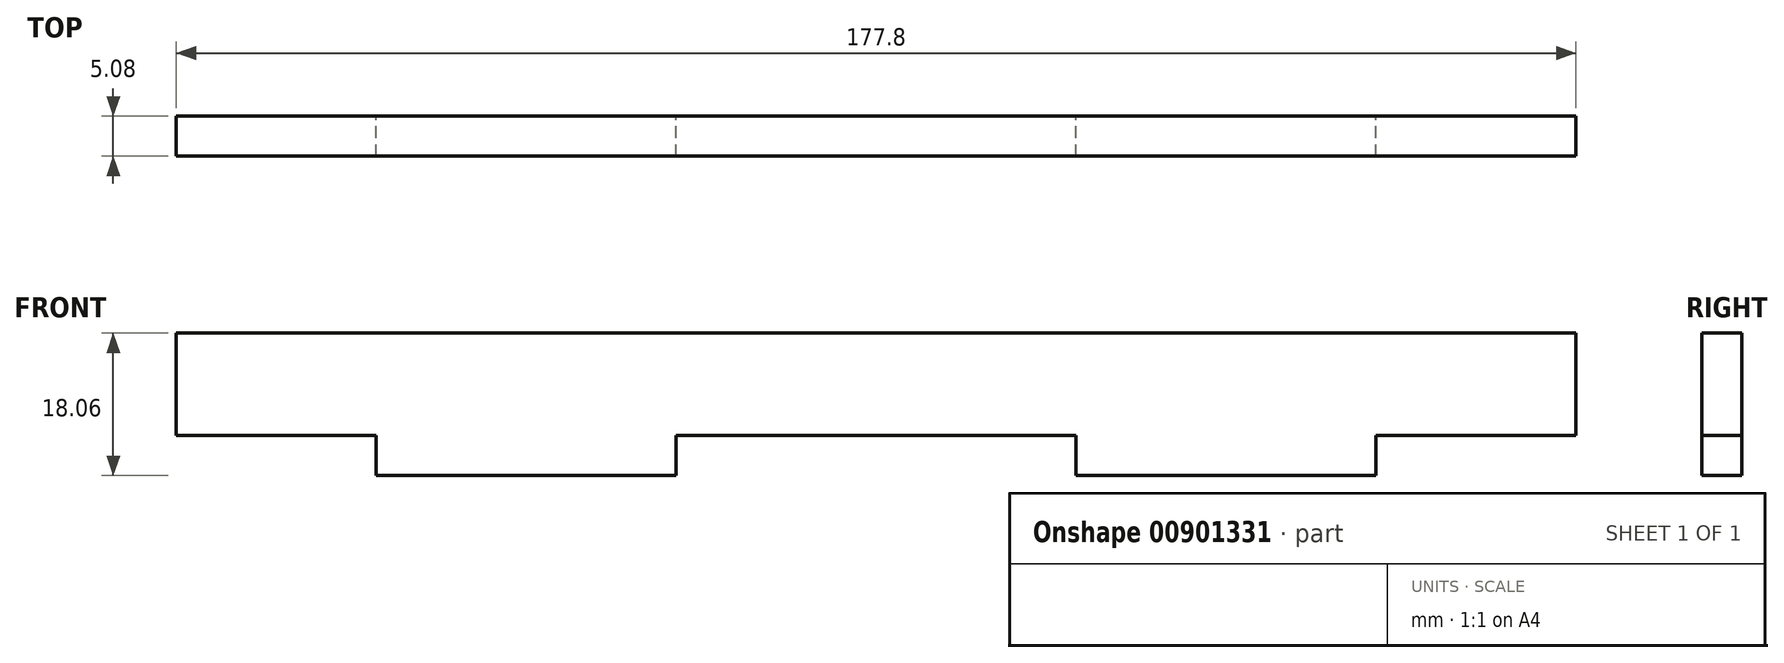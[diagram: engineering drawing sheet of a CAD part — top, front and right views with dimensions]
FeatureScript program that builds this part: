
annotation { "Feature Type Name" : "Feature", "Feature Type Description" : "" }
export const myFeature = defineFeature(function(context is Context, id is Id, definition is map)
    precondition{}
    {
        {
            var Q0;
            Q0=qCreatedBy(makeId("Front.planeOp"),FACE);
            var sketch = newSketch(context, id + "F0", { "sketchPlane" : qUnion([Q0])});
            skLineSegment(sketch, "E0", {"start": v(0, 0) * mm, "end": v(-25.4, 0) * mm});
            skLineSegment(sketch, "E1", {"start": v(-25.4, 0) * mm, "end": v(-25.4, -5.08) * mm});
            skLineSegment(sketch, "E2", {"start": v(-25.4, -5.08) * mm, "end": v(-63.5, -5.08) * mm});
            skLineSegment(sketch, "E3", {"start": v(-63.5, -5.08) * mm, "end": v(-63.5, 0) * mm});
            skLineSegment(sketch, "E4.MirrorCS", {"start": v(0, 0) * mm, "end": v(25.4, 0) * mm});
            skLineSegment(sketch, "E5.MirrorCS", {"start": v(25.4, 0) * mm, "end": v(25.4, -5.08) * mm});
            skLineSegment(sketch, "E6.MirrorCS", {"start": v(25.4, -5.08) * mm, "end": v(63.5, -5.08) * mm});
            skLineSegment(sketch, "E7.MirrorCS", {"start": v(63.5, -5.08) * mm, "end": v(63.5, 0) * mm});
            skLineSegment(sketch, "E8", {"start": v(-88.9, 3.17) * mm, "end": v(-88.9, 6.34) * mm});
            skLineSegment(sketch, "E9.MirrorCS", {"start": v(88.9, 3.17) * mm, "end": v(88.9, 6.34) * mm});
            skLineSegment(sketch, "E10", {"start": v(-88.9, 3.17) * mm, "end": v(-88.9, 0) * mm});
            skLineSegment(sketch, "E11", {"start": v(-88.9, 0) * mm, "end": v(-63.5, 0) * mm});
            skLineSegment(sketch, "E12.MirrorCS", {"start": v(88.9, 0) * mm, "end": v(63.5, 0) * mm});
            skLineSegment(sketch, "E13.MirrorCS", {"start": v(88.9, 3.17) * mm, "end": v(88.9, 0) * mm});
            skLineSegment(sketch, "E14", {"start": v(-88.9, 6.34) * mm, "end": v(-88.9, 12.98) * mm});
            skLineSegment(sketch, "E15.bottom", {"start": v(-88.9, 12.98) * mm, "end": v(88.9, 12.98) * mm});
            skLineSegment(sketch, "E15.left", {"start": v(-88.9, 12.98) * mm, "end": v(-88.9, 6.34) * mm});
            skLineSegment(sketch, "E15.right", {"start": v(88.9, 12.98) * mm, "end": v(88.9, 6.34) * mm});
            skPoint(sketch, "E16.orphan", {"position": v(0, 6.34) * mm});
            skSolve(sketch);
        }
        {
            var Q0;
            Q0=makeQuery(id+"F0.imprint","IMPRINT",FACE,{"disambiguationData":[TD([[makeQuery(id+"F0.imprint","IMPRINT",EDGE,{"derivedFrom":sQuery(id+"F0.wireOp",EDGE,"E0")}),-1.0]])]});
            var Q1;
            {var subQ4=sQuery(id+"F0.wireOp",EDGE,"ApXQHCtx-X79m-1rQq-XPcc-jefhjmjpASKC");Q1=makeQuery(id+"F0.imprint","IMPRINT",FACE,{"disambiguationData":[TD([[makeQuery(id+"F0.imprint","IMPRINT",EDGE,{"derivedFrom":subQ4}),-1.0]])]});}
            var Q2;
            {var subQ0=sQuery(id+"F0.wireOp",EDGE,"E9.MirrorCS");Q2=makeQuery(id+"F0.imprint","IMPRINT",FACE,{"disambiguationData":[TD([[makeQuery(id+"F0.imprint","IMPRINT",EDGE,{"derivedFrom":subQ0}),1.0]])]});}
            var Q3;
            {var subQ0=sQuery(id+"F0.wireOp",EDGE,"BGj7CvFe-oPBX-5Qkt-ev24-Lxmg3jkM7qoC");Q3=makeQuery(id+"F0.imprint","IMPRINT",FACE,{"disambiguationData":[TD([[makeQuery(id+"F0.imprint","IMPRINT",EDGE,{"derivedFrom":subQ0}),1.0]])]});}
            extrude(context, id + "F1", {"entities" : qUnion([Q0, Q1, Q2, Q3]), "depth" : 5.08 * mm, "offsetDistance" : 25.4 * mm});
        }
    });
